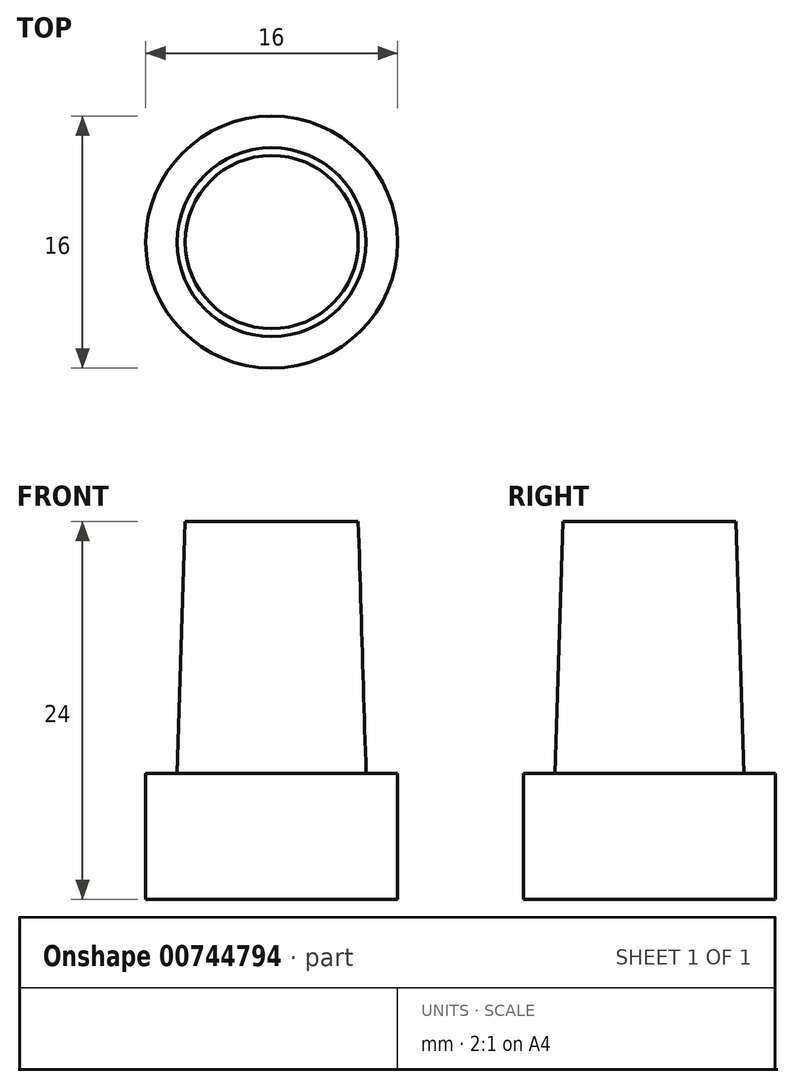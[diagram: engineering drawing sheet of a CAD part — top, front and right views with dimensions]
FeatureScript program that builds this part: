
annotation { "Feature Type Name" : "Feature", "Feature Type Description" : "" }
export const myFeature = defineFeature(function(context is Context, id is Id, definition is map)
    precondition{}
    {
        {
            var Q0;
            Q0=qCreatedBy(makeId("Top.planeOp"),FACE);
            var sketch = newSketch(context, id + "F0", { "sketchPlane" : qUnion([Q0])});
            skCircle(sketch, "E0", {"center": v(0, 0) * mm, "radius": 8 * mm});
            skSolve(sketch);
        }
        {
            var Q0;
            Q0 = qSketchRegion(id + "F0", true);
            extrude(context, id + "F1", {"entities" : qUnion([Q0]), "depth" : 8 * mm, "offsetDistance" : 25 * mm});
        }
        {
            var Q0;
            Q0=makeQuery(id+"F1.opExtrude","CAP_FACE",FACE,{"disambiguationData":[OSD([sQuery(id+"F0.wireOp",EDGE,"E0")])],"isStart":false});
            var sketch = newSketch(context, id + "F2", { "sketchPlane" : qUnion([Q0])});
            skCircle(sketch, "E1", {"center": v(0, 0) * mm, "radius": 6 * mm});
            skSolve(sketch);
        }
        {
            var Q0;
            Q0=makeQuery(id+"F2.imprint","IMPRINT",FACE,{"disambiguationData":[TD([[makeQuery(id+"F2.imprint","IMPRINT",EDGE,{"derivedFrom":sQuery(id+"F2.wireOp",EDGE,"E1")}),1.0]])]});
            cPlane(context, id + "F3", {"entities" : qUnion([Q0]), "cplaneType" : CPlaneType.OFFSET, "offset" : 16 * mm, "width" : 150 * mm, "height" : 150 * mm});
        }
        {
            var Q0;
            Q0=qCreatedBy(id+"F3.planeOp",FACE);
            var sketch = newSketch(context, id + "F4", { "sketchPlane" : qUnion([Q0])});
            skCircle(sketch, "E2", {"center": v(0, 0) * mm, "radius": 5.5 * mm});
            skSolve(sketch);
        }
        {
            var Q1;
            Q1=makeQuery(id+"F2.imprint","IMPRINT",FACE,{"disambiguationData":[TD([[makeQuery(id+"F2.imprint","IMPRINT",EDGE,{"derivedFrom":sQuery(id+"F2.wireOp",EDGE,"E1")}),1.0]])]});
            var Q2;
            Q2=makeQuery(id+"F4.imprint","IMPRINT",FACE,{"disambiguationData":[TD([[makeQuery(id+"F4.imprint","IMPRINT",EDGE,{"derivedFrom":sQuery(id+"F4.wireOp",EDGE,"E2")}),1.0]])]});
            loft(context, id + "F5", {"operationType" : NewBodyOperationType.ADD, "sheetProfilesArray" : [{ "sheetProfileEntities" : qUnion([Q1]) }, { "sheetProfileEntities" : qUnion([Q2]) }]});
        }
    });
